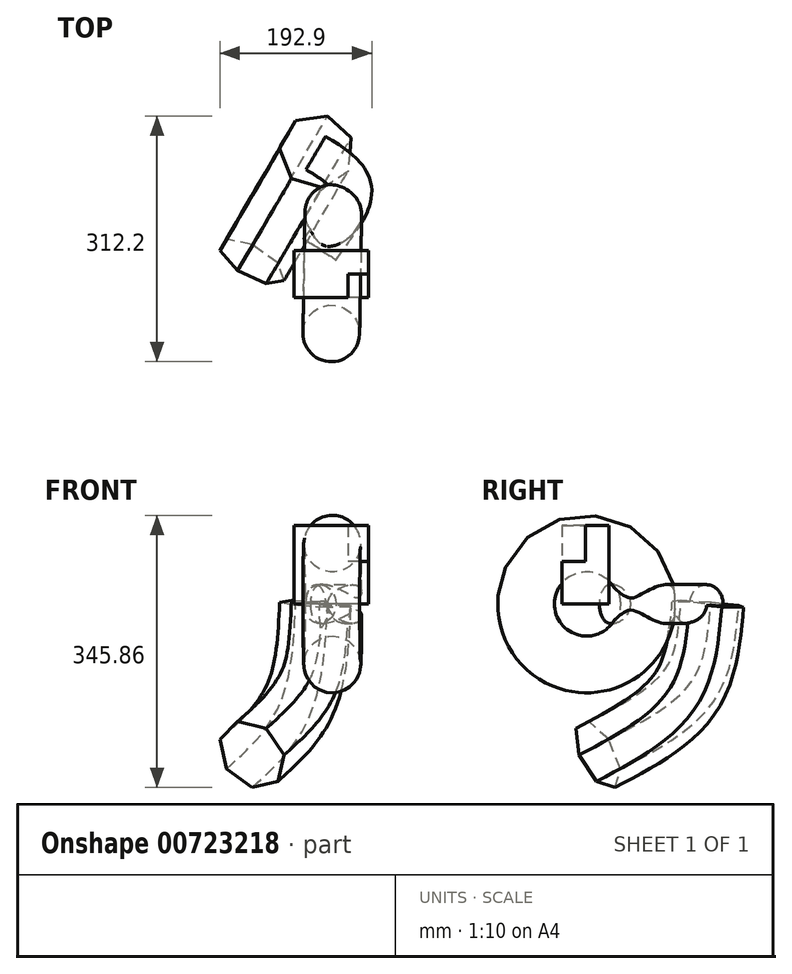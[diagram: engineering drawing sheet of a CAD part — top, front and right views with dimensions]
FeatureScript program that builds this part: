
annotation { "Feature Type Name" : "Feature", "Feature Type Description" : "" }
export const myFeature = defineFeature(function(context is Context, id is Id, definition is map)
    precondition{}
    {
        {
            var Q0;
            Q0=qCreatedBy(makeId("Top.planeOp"),FACE);
            var sketch = newSketch(context, id + "F0", { "sketchPlane" : qUnion([Q0])});
            skLineSegment(sketch, "E0.bottom", {"start": v(47.49, -29.93) * mm, "end": v(-47.49, -29.93) * mm});
            skLineSegment(sketch, "E0.top", {"start": v(47.49, 29.93) * mm, "end": v(-47.49, 29.93) * mm});
            skLineSegment(sketch, "E0.left", {"start": v(47.49, -29.93) * mm, "end": v(47.49, 29.93) * mm});
            skLineSegment(sketch, "E0.right", {"start": v(-47.49, -29.93) * mm, "end": v(-47.49, 29.93) * mm});
            skPoint(sketch, "E0.middle", {"position": v(0, 0) * mm});
            skSolve(sketch);
        }
        {
            var Q0;
            Q0=makeQuery(id+"F0.imprint","IMPRINT",FACE,{"disambiguationData":[TD([[makeQuery(id+"F0.imprint","IMPRINT",EDGE,{"derivedFrom":sQuery(id+"F0.wireOp",EDGE,"E0.bottom")}),-1.0]])]});
            extrude(context, id + "F1", {"entities" : qUnion([Q0]), "depth" : 100 * mm, "offsetDistance" : 25 * mm});
        }
        {
            var Q0;
            Q0=makeQuery(id+"F1.opExtrude","CAP_FACE",FACE,{"disambiguationData":[OSD([sQuery(id+"F0.wireOp",EDGE,"E0.bottom"),sQuery(id+"F0.wireOp",EDGE,"E0.top"),sQuery(id+"F0.wireOp",EDGE,"E0.left"),sQuery(id+"F0.wireOp",EDGE,"E0.right")])],"isStart":false});
            var sketch = newSketch(context, id + "F2", { "sketchPlane" : qUnion([Q0])});
            skCircle(sketch, "E1", {"center": v(-16.3, -2.7) * mm, "radius": 25 * mm});
            skLineSegment(sketch, "E2.bottom", {"start": v(73.69, 0) * mm, "end": v(21.3, 0) * mm});
            skLineSegment(sketch, "E2.top", {"start": v(73.69, -59.87) * mm, "end": v(21.3, -59.87) * mm});
            skLineSegment(sketch, "E2.left", {"start": v(73.69, 0) * mm, "end": v(73.69, -59.87) * mm});
            skLineSegment(sketch, "E2.right", {"start": v(21.3, 0) * mm, "end": v(21.3, -59.87) * mm});
            skPoint(sketch, "E2.middle", {"position": v(47.49, -29.93) * mm});
            skSolve(sketch);
        }
        {
            var Q0;
            {var subQ1=sQuery(id+"F2.wireOp",EDGE,"E2.top");Q0=makeQuery(id+"F2.imprint","IMPRINT",FACE,{"disambiguationData":[TD([[makeQuery(id+"F2.imprint","IMPRINT",EDGE,{"derivedFrom":subQ1}),-1.0]])]});}
            var Q1;
            {var subQ0=sQuery(id+"F2.wireOp",EDGE,"E2.right");var subQ1=sQuery(id+"F2.wireOp",EDGE,"E2.bottom");var subQ2=makeQuery(id+"F2.imprint","INTERSECT",VERTEX,{"derivedFrom":[subQ1,subQ0]});Q1=makeQuery(id+"F2.imprint","IMPRINT",FACE,{"disambiguationData":[TD([[makeQuery(id+"F2.imprint","IMPRINT",EDGE,{"disambiguationData":[TD([[subQ2,1.0]])],"derivedFrom":subQ1}),1.0]])]});}
            extrude(context, id + "F3", {"entities" : qUnion([Q0, Q1]), "operationType" : NewBodyOperationType.REMOVE, "oppositeDirection" : true, "depth" : 46 * mm, "offsetDistance" : 25 * mm});
        }
        {
            var Q0;
            Q0=qCreatedBy(makeId("Top.planeOp"),FACE);
            var sketch = newSketch(context, id + "F4", { "sketchPlane" : qUnion([Q0])});
            skCircle(sketch, "E3", {"center": v(0, -75.2) * mm, "radius": 36.03 * mm});
            skLineSegment(sketch, "E4", {"start": v(-95.22, 3.16) * mm, "end": v(96.3, 0) * mm});
            skArc(sketch, "E5", {"start": v(0, -24.24) * mm, "mid": v(-47.23, -74.02) * mm, "end": v(0, -123.8) * mm});
            skLineSegment(sketch, "E6", {"start": v(0, -123.8) * mm, "end": v(0, -24.24) * mm});
            skSolve(sketch);
        }
        {
            var Q0;
            {var subQ0=sQuery(id+"F4.wireOp",EDGE,"E6");var subQ1=sQuery(id+"F4.wireOp",EDGE,"E3");var subQ2=makeQuery(id+"F4.imprint","INTERSECT",VERTEX,{"disambiguationData":[OD(0.0)],"derivedFrom":[subQ1,subQ0]});Q0=makeQuery(id+"F4.imprint","IMPRINT",FACE,{"disambiguationData":[TD([[makeQuery(id+"F4.imprint","IMPRINT",EDGE,{"disambiguationData":[TD([[subQ2,1.0]])],"derivedFrom":subQ1}),1.0]])]});}
            var Q1;
            {var subQ0=sQuery(id+"F4.wireOp",EDGE,"E6");var subQ1=sQuery(id+"F4.wireOp",EDGE,"E3");var subQ2=makeQuery(id+"F4.imprint","INTERSECT",VERTEX,{"disambiguationData":[OD(0.0)],"derivedFrom":[subQ1,subQ0]});Q1=makeQuery(id+"F4.imprint","IMPRINT",FACE,{"disambiguationData":[TD([[makeQuery(id+"F4.imprint","IMPRINT",EDGE,{"disambiguationData":[TD([[subQ2,-1.0]])],"derivedFrom":subQ1}),1.0]])]});}
            var Q2;
            Q2=sQuery(id+"F4.wireOp",EDGE,"E4");
            revolve(context, id + "F5", {"surfaceOperationType" : NewSurfaceOperationType.NEW, "entities" : qUnion([Q0, Q1]), "axis" : qUnion([Q2]), "revolveType" : RevolveType.FULL});
        }
        {
            var Q0;
            Q0=qCreatedBy(makeId("Top.planeOp"),FACE);
            var sketch = newSketch(context, id + "F6", { "sketchPlane" : qUnion([Q0])});
            skFitSpline(sketch, "E7", {"points": [v(-14.2, 31.23) * mm, v(26.94, 108.8) * mm, v(-19.5, 154.25) * mm], "startDerivative": vector(110.7, 166.37) * mm, "endDerivative": vector(-130.36, 76.28) * mm});
            skSolve(sketch);
        }
        {
            var Q0;
            Q0=sQuery(id+"F6.wireOp",VERTEX,"E7.end");
            var Q1;
            Q1=sQuery(id+"F6.wireOp",EDGE,"E7");
            cPlane(context, id + "F7", {"entities" : qUnion([Q0, Q1]), "cplaneType" : CPlaneType.CURVE_POINT, "offset" : 25 * mm, "width" : 150 * mm, "height" : 150 * mm});
        }
        {
            var Q0;
            Q0=qCreatedBy(id+"F7.planeOp",FACE);
            var sketch = newSketch(context, id + "F8", { "sketchPlane" : qUnion([Q0])});
            skCircle(sketch, "E8", {"center": v(-122.88, 0) * mm, "radius": 24.59 * mm});
            skSolve(sketch);
        }
        {
            var Q0;
            Q0=makeQuery(id+"F8.imprint","IMPRINT",FACE,{"disambiguationData":[TD([[makeQuery(id+"F8.imprint","IMPRINT",EDGE,{"derivedFrom":sQuery(id+"F8.wireOp",EDGE,"E8")}),1.0]])]});
            var Q1;
            Q1=sQuery(id+"F6.wireOp",EDGE,"E7");
            sweep(context, id + "F9", {"profiles" : qUnion([Q0]), "path" : qUnion([Q1])});
        }
        {
            var Q0;
            Q0=qCreatedBy(id+"F7.planeOp",FACE);
            var sketch = newSketch(context, id + "F10", { "sketchPlane" : qUnion([Q0])});
            skFitSpline(sketch, "E9", {"points": [v(-125.31, 0) * mm, v(-95.33, -107.76) * mm, v(37.17, -191.26) * mm], "startDerivative": vector(24.47, -253.87) * mm, "endDerivative": vector(292.97, -132.05) * mm});
            skSolve(sketch);
        }
        {
            var Q0;
            Q0=sQuery(id+"F10.wireOp",VERTEX,"E9.end");
            var Q1;
            Q1=sQuery(id+"F10.wireOp",EDGE,"E9");
            cPlane(context, id + "F11", {"entities" : qUnion([Q0, Q1]), "cplaneType" : CPlaneType.CURVE_POINT, "offset" : 25 * mm, "width" : 150 * mm, "height" : 150 * mm});
        }
        {
            var Q0;
            Q0=qCreatedBy(id+"F11.planeOp",FACE);
            var sketch = newSketch(context, id + "F12", { "sketchPlane" : qUnion([Q0])});
            skCircle(sketch, "E10.cCircle", {"center": v(-55.05, -176.86) * mm, "radius": 42.47 * mm, "construction": true});
            skLineSegment(sketch, "E10.0", {"start": v(-91.83, -206.34) * mm, "end": v(-101.03, -166.48) * mm});
            skLineSegment(sketch, "E10.1", {"start": v(-101.03, -166.48) * mm, "end": v(-75.6, -134.44) * mm});
            skLineSegment(sketch, "E10.2", {"start": v(-75.6, -134.44) * mm, "end": v(-34.7, -134.35) * mm});
            skLineSegment(sketch, "E10.3", {"start": v(-34.7, -134.35) * mm, "end": v(-9.13, -166.26) * mm});
            skLineSegment(sketch, "E10.4", {"start": v(-9.13, -166.26) * mm, "end": v(-18.13, -206.16) * mm});
            skLineSegment(sketch, "E10.5", {"start": v(-18.13, -206.16) * mm, "end": v(-54.94, -224) * mm});
            skLineSegment(sketch, "E10.6", {"start": v(-54.94, -224) * mm, "end": v(-91.83, -206.34) * mm});
            skPoint(sketch, "E10.0.midPoint", {"position": v(-96.43, -186.41) * mm});
            skSolve(sketch);
        }
        {
            var Q0;
            Q0=makeQuery(id+"F12.imprint","IMPRINT",FACE,{"disambiguationData":[TD([[makeQuery(id+"F12.imprint","IMPRINT",EDGE,{"derivedFrom":sQuery(id+"F12.wireOp",EDGE,"E10.0")}),-1.0]])]});
            var Q1;
            Q1=sQuery(id+"F10.wireOp",EDGE,"E9");
            sweep(context, id + "F13", {"operationType" : NewBodyOperationType.ADD, "profiles" : qUnion([Q0]), "path" : qUnion([Q1])});
        }
    });
